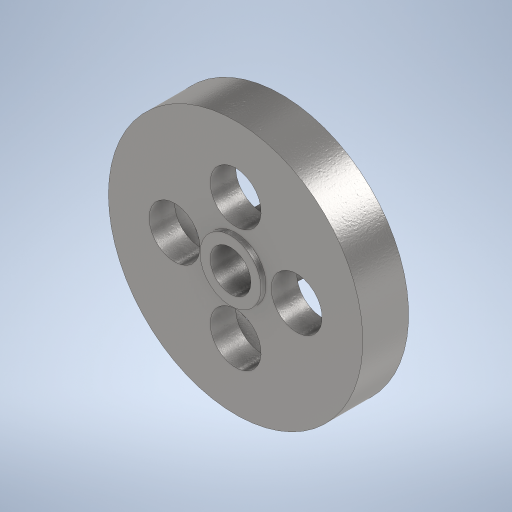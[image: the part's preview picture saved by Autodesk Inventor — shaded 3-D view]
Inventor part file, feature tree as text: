
AUTODESK INVENTOR PART (.ipt)
format: ipt  version: 2024 (Build 280153000, 153)  size: 317,440 bytes
history: native  units: mm
features: sketch x4, hole x2, revolve x1, extrude x1, pattern_circular x1
ambient origin geometry x8: Origin, YZ Plane, XZ Plane, XY Plane, X Axis, Y Axis, Z Axis, Center Point
bodies: Body1 (feature_tree)
feature tree (9):
  revolve  "Umdrehung1"
  extrude  "Extrusion3"  Depth=1.0mm
  hole  "Bohrung1"  [1 undecoded]
  hole  "Bohrung2"  [1 undecoded]
  pattern_circular  "Runde Anordnung1"  [2 undecoded]
  sketch  "Skizze4"  dims[d6=50.0mm d7=1.0mm]
  sketch  "Skizze5"  dims[d8=10.0mm d11=12.0mm]
  sketch  "Skizze6"  dims[d19=360.0deg d20=36.0mm]
  sketch  "Skizze7"  dims[d21=4.0mm d22=0.0mm d23=8.0mm d24=6.0mm d25=4.0mm d26=2.0mm d27=90.0deg d28=8.0mm d29=20.594885mm d31=24.0mm d32=10.0mm d33=6.0mm d34=4.0mm d35=2.0mm d36=90.0deg d37=8.0mm d38=20.594885mm d39=40.0mm d40=360.0deg]
note: 4 required parameter values undecoded (feature->parameter linkage not recoverable at this tier; creation-order binding heuristic only, values carry confidence <= 0.55)
